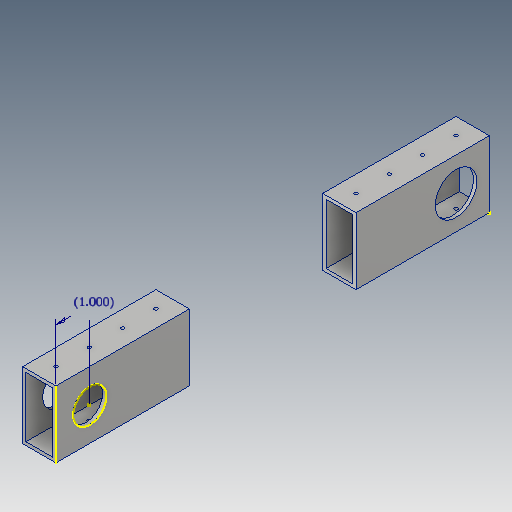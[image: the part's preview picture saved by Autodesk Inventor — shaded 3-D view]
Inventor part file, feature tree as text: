
AUTODESK INVENTOR PART (.ipt)
format: ipt  version: 2018 (Build 220112000, 112)  size: 186,880 bytes
history: native  units: in
note: dims shown in document units (in); Inventor stores cm internally (conversion verified against a paired STEP export)
features: sketch x7, extrude x4, hole x2, shell x1, projected_geometry x1
ambient origin geometry x8: Origin, YZ Plane, XZ Plane, XY Plane, X Axis, Y Axis, Z Axis, Center Point
bodies: Solid1 (feature_tree)
feature tree (15):
  extrude  "Extrusion1"  Depth=2.0in
  shell  "Shell1"  Thickness=13.0in
  hole  "Hole1"  [1 undecoded]
  hole  "Hole5"  [1 undecoded]
  extrude  "Extrusion6"  Depth=1.0in
  extrude  "Extrusion7"  Depth=1.0in
  extrude  "Extrusion8"  Depth=1.0in
  sketch  "Sketch14"  dims[d71=0.5in d72=0.75in d73=0.375in d74=0.25in d75=0.5635in d76=1.0in d77=0.8108in d78=4.0in d79=4.0in d80=1.0in d81=0.0in d82=1.25in d83=0.75in d84=0.75in d85=1.0in d86=0.0in d87=1.0in d88=1.0in d89=0.0in d90=1.0in]
  sketch  "Sketch1"  dims[d0=1.0in d1=2.0in d2=13.0in d3=0.0in]
  sketch  "Sketch2"  dims[d4=0.1in d5=0.5in]
  sketch  "Sketch10"  dims[d6=0.5in d7=14.5669in d9=1.0in d10=0.3937in d12=1.0in]
  sketch  "Sketch11"  dims[d14=0.1in d15=0.75in d16=0.375in d17=0.25in d18=0.5635in d19=2.0in d20=0.8108in d66=1.0in]
  sketch  "Sketch12"  dims[d67=1.0in d68=11.0in]
  sketch  "Sketch13"  dims[d69=1.0in d70=1.0in]
  projected_geometry  "Projected Loop3"
note: 2 required parameter values undecoded (feature->parameter linkage not recoverable at this tier; creation-order binding heuristic only, values carry confidence <= 0.55)
